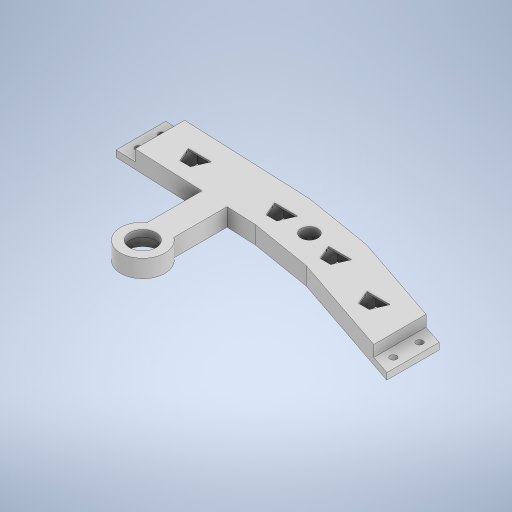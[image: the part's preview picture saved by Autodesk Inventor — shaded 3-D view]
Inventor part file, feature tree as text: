
AUTODESK INVENTOR PART (.ipt)
format: ipt  version: 2023 (Build 270158000, 158)  size: 455,680 bytes
history: native  units: mm
features: extrude x8, sketch x1
ambient origin geometry x8: Origin, YZ Plane, XZ Plane, XY Plane, X Axis, Y Axis, Z Axis, Center Point
bodies: Solid1 (feature_tree)
feature tree (9):
  sketch  "Sketch1"  dims[d75=4.9mm d76=0.0mm d77=0.5mm d78=0.0mm d263=5.2mm d264=0.0mm d265=2.9mm d266=0.0mm d269=0.5mm d270=2.9mm d271=0.0mm d272=0.0mm d273=0.5mm d274=0.0mm d282=15.1mm d283=15.1mm d286=1.175916mm d287=3.273492mm d289=15.1mm d292=4.0mm d293=6.0mm d294=4.0mm d295=4.0mm d296=2.0mm d297=2.0mm d298=4.0mm d299=6.0mm d300=4.0mm d301=4.0mm d302=2.0mm d303=2.0mm d304=5.1mm d305=2.0mm d307=15.1mm d308=7.55mm d309=7.55mm d310=3.84mm d311=3.5mm d312=7.2mm d313=7.0mm d314=3.73mm d315=0.96mm d316=2.54mm d317=2.54mm d318=2.54mm d319=1.0mm d320=1.0mm d321=1.0mm d322=1.0mm d323=7.55mm d324=7.55mm d325=3.84mm d326=3.5mm d327=7.2mm d328=7.0mm d329=3.73mm d330=0.96mm d331=2.54mm d332=2.54mm d333=2.54mm d334=1.0mm d335=1.0mm d336=1.0mm d337=1.0mm d338=7.55mm d339=7.55mm d340=3.84mm d341=3.5mm d342=7.2mm d343=7.0mm d344=3.73mm d345=0.96mm d346=2.54mm d347=2.54mm d348=2.54mm d349=1.0mm d350=1.0mm d351=1.0mm d352=1.0mm d353=7.55mm d354=7.55mm d355=3.84mm d356=3.5mm d357=7.2mm d358=7.0mm d359=3.73mm d360=0.96mm d361=2.54mm d362=2.54mm d363=2.54mm d364=1.0mm d365=1.0mm d366=1.0mm d367=1.0mm d368=30.0mm d369=8.0mm d370=10.5mm d371=13.5mm d372=8.0mm d373=0.5mm d374=4.9mm d375=0.0mm d376=0.0mm d377=0.5mm d378=1.5mm d379=0.0mm d380=0.0mm]
  extrude  "Extrusion1"  Depth=0.5mm TaperAngle=0.0deg
  extrude  "Extrusion2"  Depth=1.5mm TaperAngle=0.0deg
  extrude  "Extrusion4"  Depth=2.9mm TaperAngle=0.0deg
  extrude  "Extrusion5"  Depth=0.5mm TaperAngle=0.0deg
  extrude  "Extrusion6"  Depth=0.5mm TaperAngle=0.0deg
  extrude  "Extrusion7"  Depth=1.5mm
  extrude  "Extrusion8"  Depth=8.0mm
  extrude  "Extrusion9"  Depth=1.5mm
